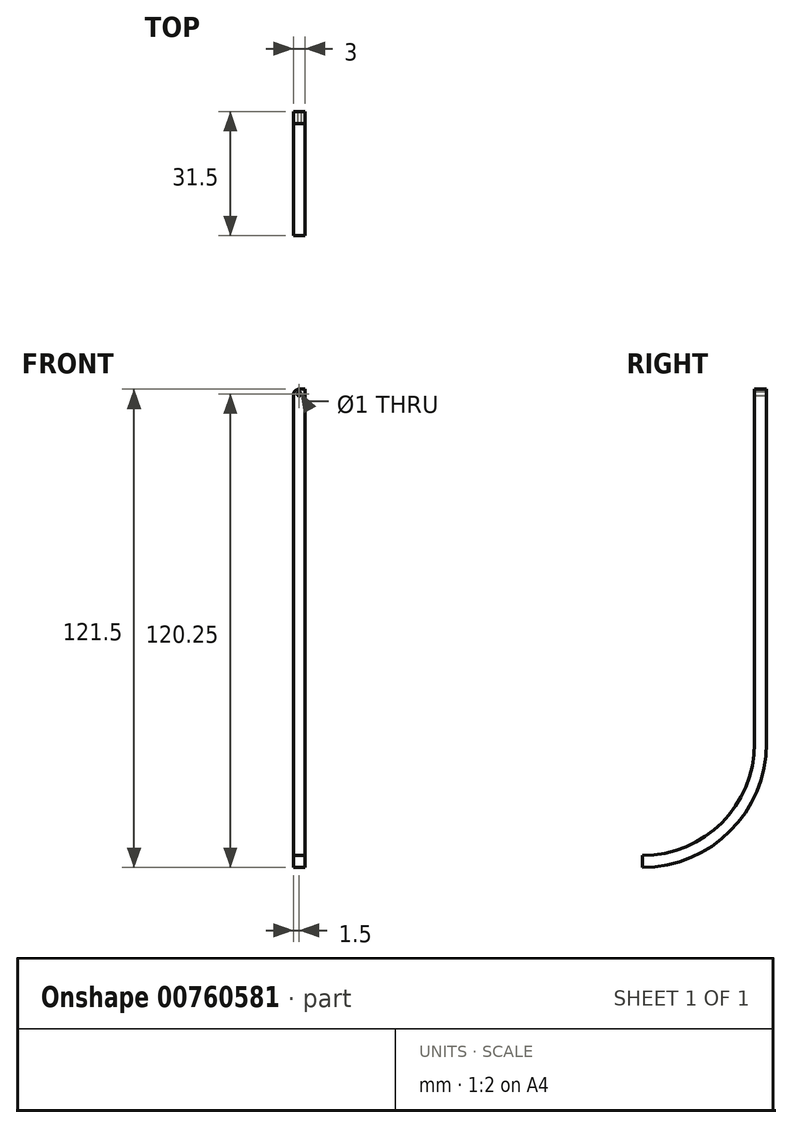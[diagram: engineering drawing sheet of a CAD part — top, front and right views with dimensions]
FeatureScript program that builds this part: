
annotation { "Feature Type Name" : "Feature", "Feature Type Description" : "" }
export const myFeature = defineFeature(function(context is Context, id is Id, definition is map)
    precondition{}
    {
        {
            var Q0;
            Q0=qCreatedBy(makeId("Right.planeOp"),FACE);
            var sketch = newSketch(context, id + "F0", { "sketchPlane" : qUnion([Q0])});
            skLineSegment(sketch, "E0", {"start": v(-1.5, 0) * mm, "end": v(1.5, 0) * mm});
            skLineSegment(sketch, "E1", {"start": v(1.5, 0) * mm, "end": v(1.5, -90) * mm});
            skLineSegment(sketch, "E2", {"start": v(-1.5, -90) * mm, "end": v(-1.5, 0) * mm});
            skLineSegment(sketch, "E3", {"start": v(-30, -118.5) * mm, "end": v(-30, -121.5) * mm});
            skArc(sketch, "E4", {"start": v(-1.5, -90) * mm, "mid": v(-9.85, -110.15) * mm, "end": v(-30, -118.5) * mm});
            skArc(sketch, "E5", {"start": v(1.5, -90) * mm, "mid": v(-7.73, -112.27) * mm, "end": v(-30, -121.5) * mm});
            skPoint(sketch, "E6.end.orphan", {"position": v(-1.5, -120) * mm});
            skSolve(sketch);
        }
        {
            var Q0;
            Q0=qCreatedBy(makeId("Front.planeOp"),FACE);
            var sketch = newSketch(context, id + "F1", { "sketchPlane" : qUnion([Q0])});
            skCircle(sketch, "E7", {"center": v(1.5, -1.25) * mm, "radius": 0.5 * mm});
            skSolve(sketch);
        }
        {
            var Q0;
            Q0 = qSketchRegion(id + "F0", true);
            extrude(context, id + "F2", {"entities" : qUnion([Q0]), "depth" : 3 * mm, "offsetDistance" : 25 * mm});
        }
        {
            var Q0;
            Q0 = qSketchRegion(id + "F1", true);
            extrude(context, id + "F3", {"entities" : qUnion([Q0]), "operationType" : NewBodyOperationType.REMOVE, "oppositeDirection" : true, "depth" : 1.5 * mm, "offsetDistance" : 25 * mm});
        }
        {
            var Q0;
            Q0 = qSketchRegion(id + "F1", true);
            extrude(context, id + "F4", {"entities" : qUnion([Q0]), "operationType" : NewBodyOperationType.REMOVE, "depth" : 1.5 * mm, "offsetDistance" : 25 * mm});
        }
        {
            var Q0;
            Q0=makeQuery(id+"F2.opExtrude","CAP_EDGE",EDGE,{"disambiguationData":[OSD([sQuery(id+"F0.wireOp",EDGE,"E0")])],"isStart":true});
            fillet(context, id + "F5", {"entities" : qUnion([Q0]), "radius" : 1.5 * mm, "tangentPropagation" : true, "allowEdgeOverflow" : false});
        }
    });
